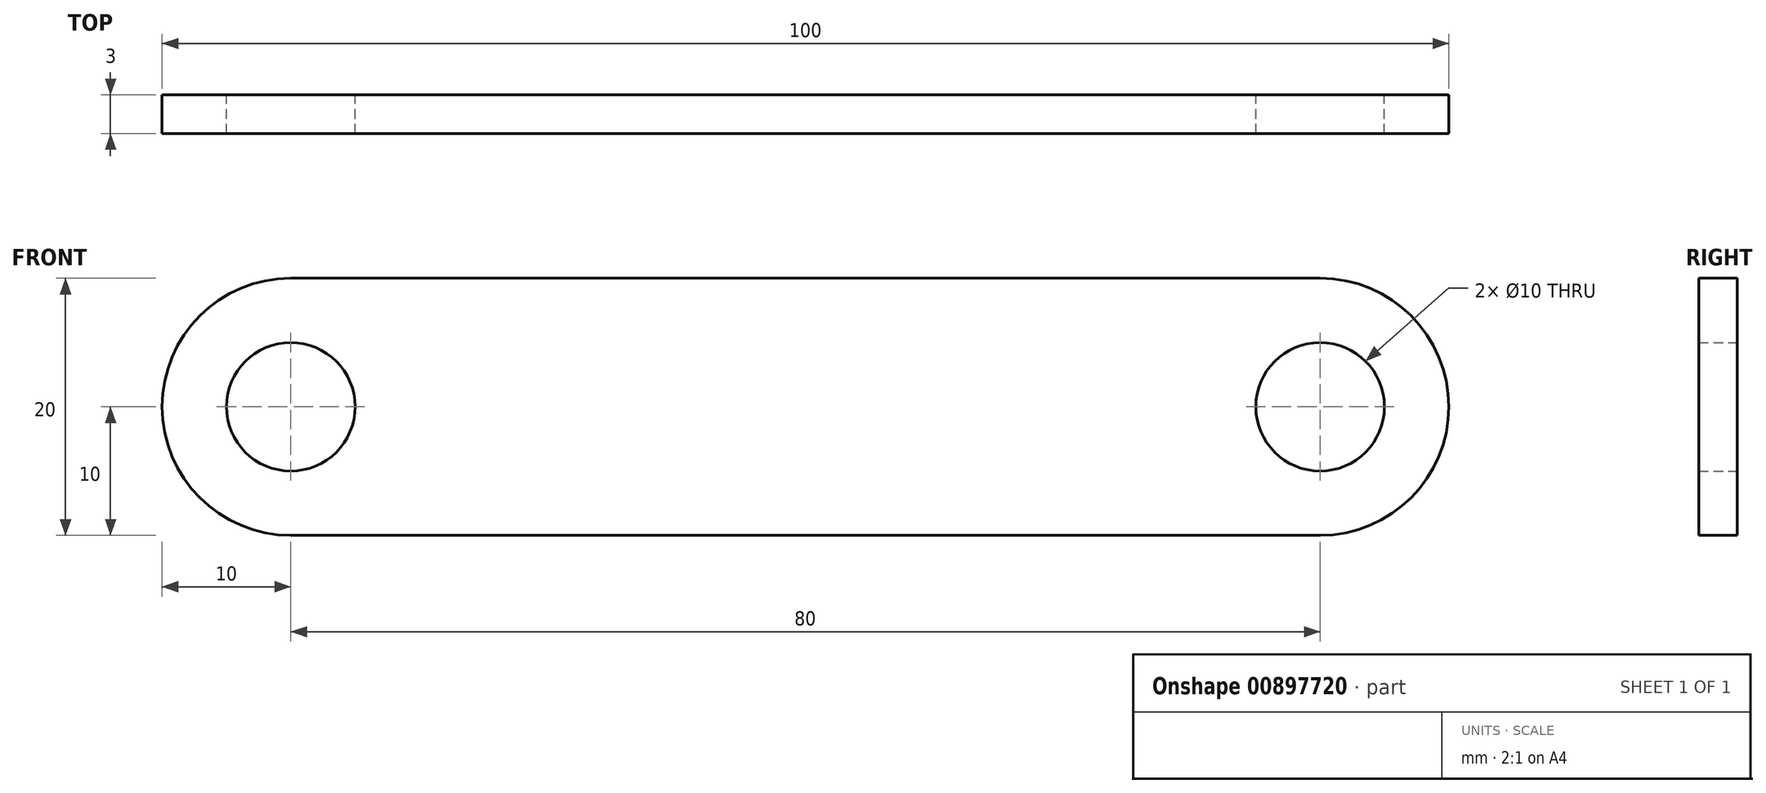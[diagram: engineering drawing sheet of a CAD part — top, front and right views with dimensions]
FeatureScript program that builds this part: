
annotation { "Feature Type Name" : "Feature", "Feature Type Description" : "" }
export const myFeature = defineFeature(function(context is Context, id is Id, definition is map)
    precondition{}
    {
        {
            var Q0;
            Q0=qCreatedBy(makeId("Front.planeOp"),FACE);
            var sketch = newSketch(context, id + "F0", { "sketchPlane" : qUnion([Q0])});
            skArc(sketch, "E0", {"start": v(0, 10) * mm, "mid": v(-10, 0) * mm, "end": v(0, -10) * mm});
            skArc(sketch, "E1", {"start": v(80, -10) * mm, "mid": v(90, 0) * mm, "end": v(80, 10) * mm});
            skLineSegment(sketch, "E2", {"start": v(0, 10) * mm, "end": v(80, 10) * mm});
            skLineSegment(sketch, "E3", {"start": v(0, -10) * mm, "end": v(80, -10) * mm});
            skCircle(sketch, "E4", {"center": v(0, 0) * mm, "radius": 5 * mm});
            skCircle(sketch, "E5", {"center": v(80, 0) * mm, "radius": 5 * mm});
            skSolve(sketch);
        }
        {
            var Q0;
            Q0 = qSketchRegion(id + "F0", true);
            extrude(context, id + "F1", {"entities" : qUnion([Q0]), "depth" : 3 * mm, "offsetDistance" : 25 * mm});
        }
    });
